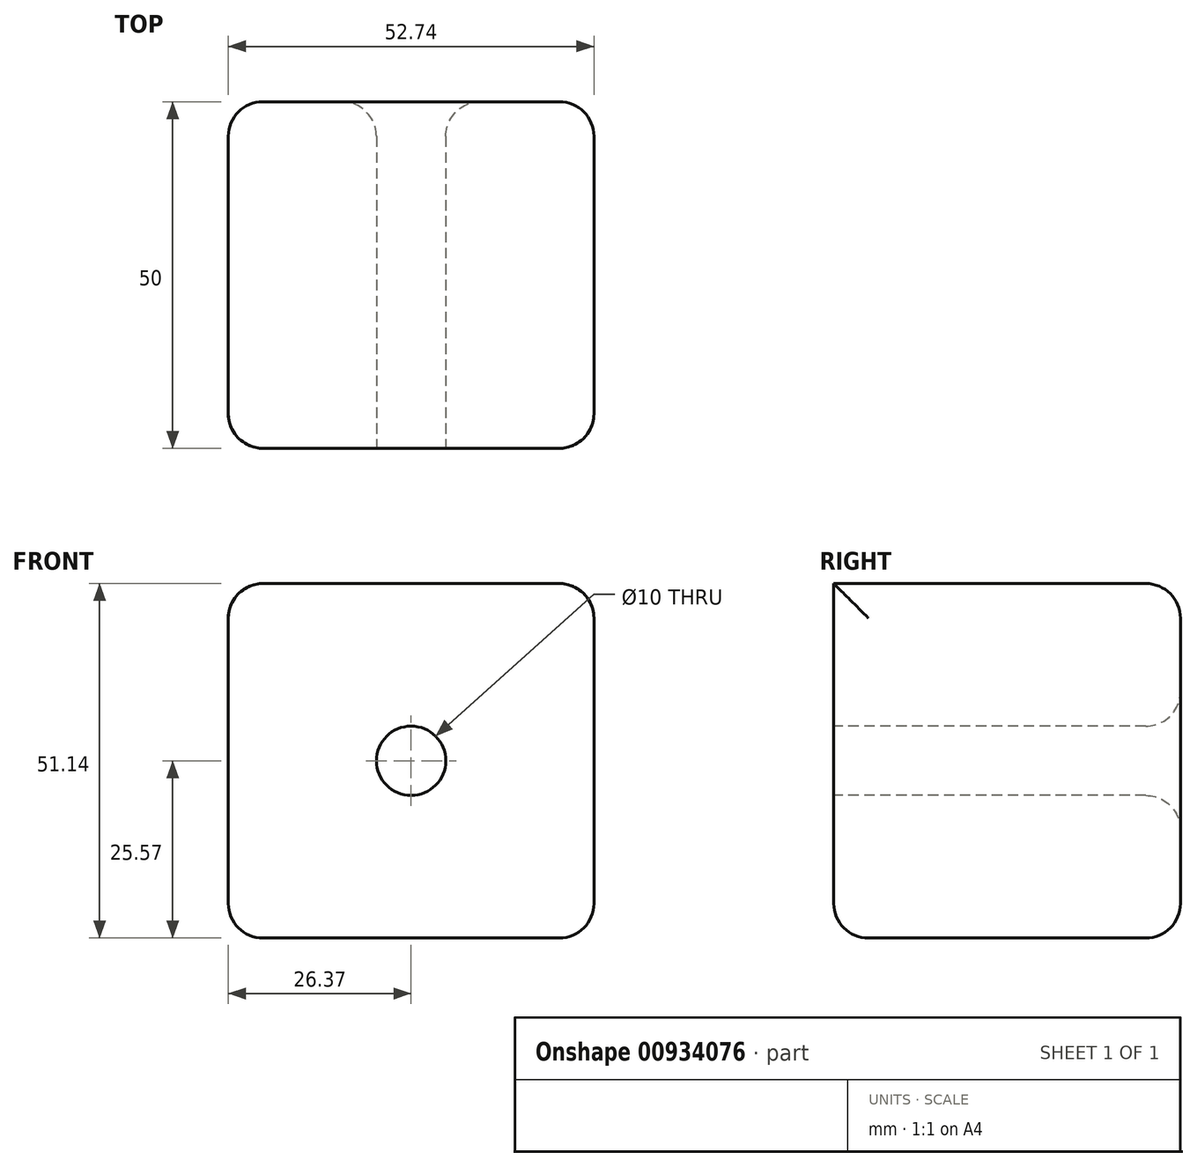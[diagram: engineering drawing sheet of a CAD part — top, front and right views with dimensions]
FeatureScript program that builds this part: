
annotation { "Feature Type Name" : "Feature", "Feature Type Description" : "" }
export const myFeature = defineFeature(function(context is Context, id is Id, definition is map)
    precondition{}
    {
        {
            var Q0;
            Q0=qCreatedBy(makeId("Front.planeOp"),FACE);
            var sketch = newSketch(context, id + "F0", { "sketchPlane" : qUnion([Q0])});
            skLineSegment(sketch, "E0.bottom", {"start": v(26.37, 25.57) * mm, "end": v(-26.37, 25.57) * mm});
            skLineSegment(sketch, "E0.top", {"start": v(26.37, -25.57) * mm, "end": v(-26.37, -25.57) * mm});
            skLineSegment(sketch, "E0.left", {"start": v(26.37, 25.57) * mm, "end": v(26.37, -25.57) * mm});
            skLineSegment(sketch, "E0.right", {"start": v(-26.37, 25.57) * mm, "end": v(-26.37, -25.57) * mm});
            skPoint(sketch, "E0.middle", {"position": v(0, 0) * mm});
            skSolve(sketch);
        }
        {
            var Q0;
            Q0 = qSketchRegion(id + "F0", true);
            extrude(context, id + "F1", {"entities" : qUnion([Q0]), "depth" : 50 * mm, "offsetDistance" : 25.4 * mm});
        }
        {
            var Q0;
            Q0=makeQuery(id+"F1.opExtrude","CAP_FACE",FACE,{"disambiguationData":[OSD([sQuery(id+"F0.wireOp",EDGE,"E0.bottom"),sQuery(id+"F0.wireOp",EDGE,"E0.top"),sQuery(id+"F0.wireOp",EDGE,"E0.left"),sQuery(id+"F0.wireOp",EDGE,"E0.right")])],"isStart":false});
            var sketch = newSketch(context, id + "F2", { "sketchPlane" : qUnion([Q0])});
            skCircle(sketch, "E1", {"center": v(0, 0) * mm, "radius": 5 * mm});
            skSolve(sketch);
        }
        {
            var Q0;
            Q0=makeQuery(id+"F2.imprint","IMPRINT",FACE,{"disambiguationData":[TD([[makeQuery(id+"F2.imprint","IMPRINT",EDGE,{"derivedFrom":sQuery(id+"F2.wireOp",EDGE,"E1")}),1.0]])]});
            extrude(context, id + "F3", {"entities" : qUnion([Q0]), "operationType" : NewBodyOperationType.REMOVE, "endBound" : BoundingType.THROUGH_ALL, "oppositeDirection" : true, "depth" : 25 * mm, "offsetDistance" : 25 * mm});
        }
        {
            var Q0;
            Q0=makeQuery(id+"F3.boolean.opBoolean","COPY",EDGE,{"derivedFrom":makeQuery(id+"F3.opExtrude","CAP_EDGE",EDGE,{"disambiguationData":[OSD([sQuery(id+"F2.wireOp",EDGE,"E1")])],"isStart":true})});
            var Q1;
            Q1=makeQuery(id+"F3.boolean.opBoolean","INTERSECT",EDGE,{"derivedFrom":[makeQuery(id+"F1.opExtrude","CAP_FACE",FACE,{"disambiguationData":[OSD([sQuery(id+"F0.wireOp",EDGE,"E0.bottom"),sQuery(id+"F0.wireOp",EDGE,"E0.top"),sQuery(id+"F0.wireOp",EDGE,"E0.left"),sQuery(id+"F0.wireOp",EDGE,"E0.right")])],"isStart":true}),makeQuery(id+"F3.opExtrude","SWEPT_FACE",FACE,{"disambiguationData":[OSD([sQuery(id+"F2.wireOp",EDGE,"E1")])]})]});
            var Q2;
            Q2=makeQuery(id+"F1.opExtrude","SWEPT_EDGE",EDGE,{"disambiguationData":[OSD([sQuery(id+"F0.wireOp",EDGE,"E0.top"),sQuery(id+"F0.wireOp",EDGE,"E0.left")])]});
            var Q3;
            Q3=makeQuery(id+"F1.opExtrude","CAP_EDGE",EDGE,{"disambiguationData":[OSD([sQuery(id+"F0.wireOp",EDGE,"E0.left")])],"isStart":false});
            var Q4;
            Q4=makeQuery(id+"F1.opExtrude","CAP_EDGE",EDGE,{"disambiguationData":[OSD([sQuery(id+"F0.wireOp",EDGE,"E0.left")])],"isStart":true});
            var Q5;
            Q5=makeQuery(id+"F1.opExtrude","SWEPT_EDGE",EDGE,{"disambiguationData":[OSD([sQuery(id+"F0.wireOp",EDGE,"E0.bottom"),sQuery(id+"F0.wireOp",EDGE,"E0.left")])]});
            var Q6;
            Q6=makeQuery(id+"F1.opExtrude","CAP_EDGE",EDGE,{"disambiguationData":[OSD([sQuery(id+"F0.wireOp",EDGE,"E0.top")])],"isStart":false});
            var Q7;
            Q7=makeQuery(id+"F1.opExtrude","CAP_EDGE",EDGE,{"disambiguationData":[OSD([sQuery(id+"F0.wireOp",EDGE,"E0.right")])],"isStart":false});
            var Q8;
            Q8=makeQuery(id+"F1.opExtrude","SWEPT_EDGE",EDGE,{"disambiguationData":[OSD([sQuery(id+"F0.wireOp",EDGE,"E0.top"),sQuery(id+"F0.wireOp",EDGE,"E0.right")])]});
            var Q9;
            Q9=makeQuery(id+"F1.opExtrude","CAP_EDGE",EDGE,{"disambiguationData":[OSD([sQuery(id+"F0.wireOp",EDGE,"E0.top")])],"isStart":true});
            var Q10;
            Q10=makeQuery(id+"F1.opExtrude","CAP_EDGE",EDGE,{"disambiguationData":[OSD([sQuery(id+"F0.wireOp",EDGE,"E0.bottom")])],"isStart":true});
            var Q11;
            Q11=makeQuery(id+"F1.opExtrude","CAP_EDGE",EDGE,{"disambiguationData":[OSD([sQuery(id+"F0.wireOp",EDGE,"E0.right")])],"isStart":true});
            var Q12;
            Q12=makeQuery(id+"F1.opExtrude","SWEPT_EDGE",EDGE,{"disambiguationData":[OSD([sQuery(id+"F0.wireOp",EDGE,"E0.bottom"),sQuery(id+"F0.wireOp",EDGE,"E0.right")])]});
            fillet(context, id + "F4", {"entities" : qUnion([Q0, Q1, Q2, Q3, Q4, Q5, Q6, Q7, Q8, Q9, Q10, Q11, Q12]), "radius" : 5 * mm, "tangentPropagation" : true, "allowEdgeOverflow" : false});
        }
    });
